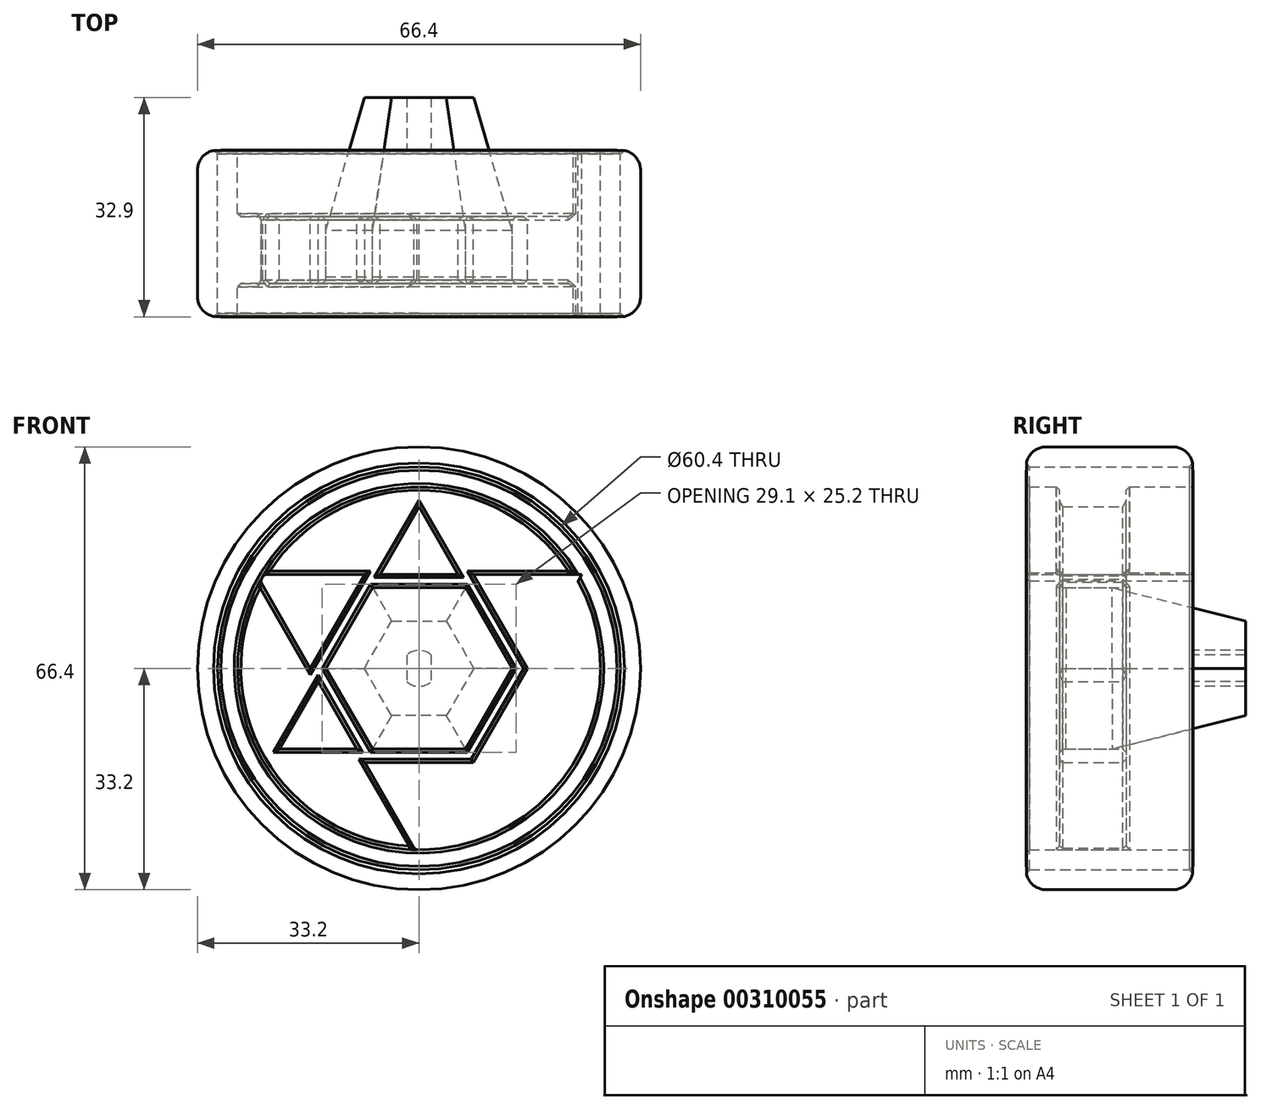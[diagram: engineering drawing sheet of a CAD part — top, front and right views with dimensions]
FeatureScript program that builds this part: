
annotation { "Feature Type Name" : "Feature", "Feature Type Description" : "" }
export const myFeature = defineFeature(function(context is Context, id is Id, definition is map)
    precondition{}
    {
        {
            var Q0;
            Q0=qCreatedBy(makeId("Front.planeOp"),FACE);
            var sketch = newSketch(context, id + "F0", { "sketchPlane" : qUnion([Q0])});
            skCircle(sketch, "E0", {"center": v(0, 0) * mm, "radius": 33.2 * mm});
            skCircle(sketch, "E1.0", {"center": v(0, 0) * mm, "radius": 30.2 * mm});
            skCircle(sketch, "E2.0", {"center": v(0, 0) * mm, "radius": 28.2 * mm});
            skCircle(sketch, "E3.0", {"center": v(0, 0) * mm, "radius": 27.2 * mm});
            skCircle(sketch, "E4.cCircle", {"center": v(0, 0) * mm, "radius": 28.2 * mm, "construction": true});
            skLineSegment(sketch, "E4.0", {"start": v(0, -28.2) * mm, "end": v(-24.42, 14.1) * mm});
            skLineSegment(sketch, "E4.1", {"start": v(-24.42, 14.1) * mm, "end": v(24.42, 14.1) * mm});
            skLineSegment(sketch, "E4.2", {"start": v(24.42, 14.1) * mm, "end": v(0, -28.2) * mm});
            skLineSegment(sketch, "E5.0", {"start": v(0, 28.2) * mm, "end": v(24.42, -14.1) * mm});
            skLineSegment(sketch, "E5.1", {"start": v(24.42, -14.1) * mm, "end": v(-24.42, -14.1) * mm});
            skLineSegment(sketch, "E5.2", {"start": v(-24.42, -14.1) * mm, "end": v(0, 28.2) * mm});
            skLineSegment(sketch, "E6.0", {"start": v(0, 24.2) * mm, "end": v(20.96, -12.1) * mm});
            skLineSegment(sketch, "E6.1", {"start": v(-20.96, -12.1) * mm, "end": v(0, 24.2) * mm});
            skLineSegment(sketch, "E6.2", {"start": v(20.96, -12.1) * mm, "end": v(-20.96, -12.1) * mm});
            skLineSegment(sketch, "E7.0", {"start": v(-20.96, 12.1) * mm, "end": v(20.96, 12.1) * mm});
            skLineSegment(sketch, "E7.1", {"start": v(0, -24.2) * mm, "end": v(-20.96, 12.1) * mm});
            skLineSegment(sketch, "E7.2", {"start": v(20.96, 12.1) * mm, "end": v(0, -24.2) * mm});
            skPoint(sketch, "E8.trimOffspring.end.orphan", {"position": v(-10.48, 6.05) * mm});
            skPoint(sketch, "E9.left.start.orphan", {"position": v(-12.04, 3.35) * mm});
            skPoint(sketch, "E10.orphan", {"position": v(-12.04, -3.35) * mm});
            skPoint(sketch, "E11.left.start.orphan", {"position": v(-10.48, -6.05) * mm});
            skPoint(sketch, "E9.bottom.end.orphan", {"position": v(12.04, 3.35) * mm});
            skPoint(sketch, "E12.trimOffspring.end.orphan", {"position": v(10.48, 6.05) * mm});
            skPoint(sketch, "E11.right.start.orphan", {"position": v(10.48, -6.05) * mm});
            skPoint(sketch, "E9.top.end.orphan", {"position": v(12.04, -3.35) * mm});
            skSolve(sketch);
        }
        {
            var Q0;
            Q0=makeQuery(id+"F0.imprint","IMPRINT",FACE,{"disambiguationData":[TD([[makeQuery(id+"F0.imprint","IMPRINT",EDGE,{"derivedFrom":sQuery(id+"F0.wireOp",EDGE,"E0")}),1.0]])]});
            extrude(context, id + "F1", {"entities" : qUnion([Q0]), "depth" : 25 * mm});
        }
        {
            var Q0;
            Q0=makeQuery(id+"F0.imprint","IMPRINT",FACE,{"disambiguationData":[TD([[makeQuery(id+"F0.imprint","IMPRINT",EDGE,{"derivedFrom":sQuery(id+"F0.wireOp",EDGE,"E1.0")}),1.0]])]});
            var Q1;
            {var subQ0=sQuery(id+"F0.wireOp",EDGE,"E4.1");var subQ5=sQuery(id+"F0.wireOp",EDGE,"E3.0");var subQ6=makeQuery(id+"F0.imprint","INTERSECT",VERTEX,{"disambiguationData":[OD(0.0)],"derivedFrom":[subQ5,subQ0]});Q1=makeQuery(id+"F0.imprint","IMPRINT",FACE,{"disambiguationData":[TD([[makeQuery(id+"F0.imprint","IMPRINT",EDGE,{"disambiguationData":[TD([[subQ6,-1.0]])],"derivedFrom":subQ5}),-1.0]])]});}
            var Q2;
            {var subQ3=sQuery(id+"F0.wireOp",EDGE,"E5.2");var subQ5=sQuery(id+"F0.wireOp",EDGE,"E3.0");var subQ6=makeQuery(id+"F0.imprint","INTERSECT",VERTEX,{"disambiguationData":[OD(0.0)],"derivedFrom":[subQ5,subQ3]});Q2=makeQuery(id+"F0.imprint","IMPRINT",FACE,{"disambiguationData":[TD([[makeQuery(id+"F0.imprint","IMPRINT",EDGE,{"disambiguationData":[TD([[subQ6,-1.0]])],"derivedFrom":subQ5}),-1.0]])]});}
            var Q3;
            {var subQ0=sQuery(id+"F0.wireOp",EDGE,"E4.0");var subQ5=sQuery(id+"F0.wireOp",EDGE,"E3.0");var subQ6=makeQuery(id+"F0.imprint","INTERSECT",VERTEX,{"disambiguationData":[OD(0.0)],"derivedFrom":[subQ5,subQ0]});Q3=makeQuery(id+"F0.imprint","IMPRINT",FACE,{"disambiguationData":[TD([[makeQuery(id+"F0.imprint","IMPRINT",EDGE,{"disambiguationData":[TD([[subQ6,-1.0]])],"derivedFrom":subQ5}),-1.0]])]});}
            var Q4;
            {var subQ3=sQuery(id+"F0.wireOp",EDGE,"E5.1");var subQ5=sQuery(id+"F0.wireOp",EDGE,"E3.0");var subQ7=makeQuery(id+"F0.imprint","INTERSECT",VERTEX,{"disambiguationData":[OD(0.0)],"derivedFrom":[subQ5,subQ3]});Q4=makeQuery(id+"F0.imprint","IMPRINT",FACE,{"disambiguationData":[TD([[makeQuery(id+"F0.imprint","IMPRINT",EDGE,{"disambiguationData":[TD([[subQ7,-1.0]])],"derivedFrom":subQ5}),-1.0]])]});}
            var Q5;
            {var subQ0=sQuery(id+"F0.wireOp",EDGE,"E4.2");var subQ5=sQuery(id+"F0.wireOp",EDGE,"E3.0");var subQ6=makeQuery(id+"F0.imprint","INTERSECT",VERTEX,{"disambiguationData":[OD(1.0)],"derivedFrom":[subQ5,subQ0]});Q5=makeQuery(id+"F0.imprint","IMPRINT",FACE,{"disambiguationData":[TD([[makeQuery(id+"F0.imprint","IMPRINT",EDGE,{"disambiguationData":[TD([[subQ6,-1.0]])],"derivedFrom":subQ5}),-1.0]])]});}
            var Q6;
            {var subQ0=sQuery(id+"F0.wireOp",EDGE,"E4.2");var subQ5=sQuery(id+"F0.wireOp",EDGE,"E3.0");var subQ6=makeQuery(id+"F0.imprint","INTERSECT",VERTEX,{"disambiguationData":[OD(0.0)],"derivedFrom":[subQ5,subQ0]});Q6=makeQuery(id+"F0.imprint","IMPRINT",FACE,{"disambiguationData":[TD([[makeQuery(id+"F0.imprint","IMPRINT",EDGE,{"disambiguationData":[TD([[subQ6,1.0]])],"derivedFrom":subQ5}),-1.0]])]});}
            var Q7;
            {var subQ0=sQuery(id+"F0.wireOp",EDGE,"E5.1");var subQ1=sQuery(id+"F0.wireOp",EDGE,"E3.0");var subQ2=makeQuery(id+"F0.imprint","INTERSECT",VERTEX,{"disambiguationData":[OD(1.0)],"derivedFrom":[subQ1,subQ0]});Q7=makeQuery(id+"F0.imprint","IMPRINT",FACE,{"disambiguationData":[TD([[makeQuery(id+"F0.imprint","IMPRINT",EDGE,{"disambiguationData":[TD([[subQ2,-1.0]])],"derivedFrom":subQ1}),-1.0]])]});}
            var Q8;
            {var subQ0=sQuery(id+"F0.wireOp",EDGE,"E4.0");var subQ1=sQuery(id+"F0.wireOp",EDGE,"E3.0");var subQ2=makeQuery(id+"F0.imprint","INTERSECT",VERTEX,{"disambiguationData":[OD(1.0)],"derivedFrom":[subQ1,subQ0]});Q8=makeQuery(id+"F0.imprint","IMPRINT",FACE,{"disambiguationData":[TD([[makeQuery(id+"F0.imprint","IMPRINT",EDGE,{"disambiguationData":[TD([[subQ2,-1.0]])],"derivedFrom":subQ1}),-1.0]])]});}
            var Q9;
            {var subQ0=sQuery(id+"F0.wireOp",EDGE,"E4.1");var subQ1=sQuery(id+"F0.wireOp",EDGE,"E3.0");var subQ2=makeQuery(id+"F0.imprint","INTERSECT",VERTEX,{"disambiguationData":[OD(0.0)],"derivedFrom":[subQ1,subQ0]});Q9=makeQuery(id+"F0.imprint","IMPRINT",FACE,{"disambiguationData":[TD([[makeQuery(id+"F0.imprint","IMPRINT",EDGE,{"disambiguationData":[TD([[subQ2,1.0]])],"derivedFrom":subQ1}),-1.0]])]});}
            var Q10;
            {var subQ0=sQuery(id+"F0.wireOp",EDGE,"E5.0");var subQ1=sQuery(id+"F0.wireOp",EDGE,"E3.0");var subQ2=makeQuery(id+"F0.imprint","INTERSECT",VERTEX,{"disambiguationData":[OD(0.0)],"derivedFrom":[subQ1,subQ0]});Q10=makeQuery(id+"F0.imprint","IMPRINT",FACE,{"disambiguationData":[TD([[makeQuery(id+"F0.imprint","IMPRINT",EDGE,{"disambiguationData":[TD([[subQ2,-1.0]])],"derivedFrom":subQ1}),-1.0]])]});}
            var Q11;
            {var subQ0=sQuery(id+"F0.wireOp",EDGE,"E4.1");var subQ1=sQuery(id+"F0.wireOp",EDGE,"E3.0");var subQ2=makeQuery(id+"F0.imprint","INTERSECT",VERTEX,{"disambiguationData":[OD(1.0)],"derivedFrom":[subQ1,subQ0]});Q11=makeQuery(id+"F0.imprint","IMPRINT",FACE,{"disambiguationData":[TD([[makeQuery(id+"F0.imprint","IMPRINT",EDGE,{"disambiguationData":[TD([[subQ2,-1.0]])],"derivedFrom":subQ1}),-1.0]])]});}
            var Q12;
            {var subQ0=sQuery(id+"F0.wireOp",EDGE,"E5.2");var subQ1=sQuery(id+"F0.wireOp",EDGE,"E3.0");var subQ2=makeQuery(id+"F0.imprint","INTERSECT",VERTEX,{"disambiguationData":[OD(1.0)],"derivedFrom":[subQ1,subQ0]});Q12=makeQuery(id+"F0.imprint","IMPRINT",FACE,{"disambiguationData":[TD([[makeQuery(id+"F0.imprint","IMPRINT",EDGE,{"disambiguationData":[TD([[subQ2,-1.0]])],"derivedFrom":subQ1}),-1.0]])]});}
            extrude(context, id + "F2", {"entities" : qUnion([Q0, Q1, Q2, Q3, Q4, Q5, Q6, Q7, Q8, Q9, Q10, Q11, Q12]), "depth" : 25 * mm});
        }
        {
            var Q0;
            {var subQ3=sQuery(id+"F0.wireOp",EDGE,"E5.0");var subQ7=sQuery(id+"F0.wireOp",EDGE,"E3.0");var subQ8=makeQuery(id+"F0.imprint","INTERSECT",VERTEX,{"disambiguationData":[OD(0.0)],"derivedFrom":[subQ7,subQ3]});Q0=makeQuery(id+"F0.imprint","IMPRINT",FACE,{"disambiguationData":[TD([[makeQuery(id+"F0.imprint","IMPRINT",EDGE,{"disambiguationData":[TD([[subQ8,-1.0]])],"derivedFrom":subQ7}),1.0]])]});}
            var Q1;
            {var subQ1=sQuery(id+"F0.wireOp",EDGE,"E4.1");var subQ6=sQuery(id+"F0.wireOp",EDGE,"E3.0");var subQ12=makeQuery(id+"F0.imprint","INTERSECT",VERTEX,{"disambiguationData":[OD(0.0)],"derivedFrom":[subQ6,subQ1]});Q1=makeQuery(id+"F0.imprint","IMPRINT",FACE,{"disambiguationData":[TD([[makeQuery(id+"F0.imprint","IMPRINT",EDGE,{"disambiguationData":[TD([[subQ12,1.0]])],"derivedFrom":subQ6}),1.0]])]});}
            var Q2;
            {var subQ0=sQuery(id+"F0.wireOp",EDGE,"E6.0");var subQ1=sQuery(id+"F0.wireOp",EDGE,"E4.1");var subQ2=makeQuery(id+"F0.imprint","INTERSECT",VERTEX,{"derivedFrom":[subQ1,subQ0]});Q2=makeQuery(id+"F0.imprint","IMPRINT",FACE,{"disambiguationData":[TD([[makeQuery(id+"F0.imprint","IMPRINT",EDGE,{"disambiguationData":[TD([[subQ2,-1.0]])],"derivedFrom":subQ1}),-1.0]])]});}
            var Q3;
            {var subQ1=sQuery(id+"F0.wireOp",EDGE,"E3.0");var subQ7=sQuery(id+"F0.wireOp",EDGE,"E5.2");var subQ11=makeQuery(id+"F0.imprint","INTERSECT",VERTEX,{"disambiguationData":[OD(1.0)],"derivedFrom":[subQ1,subQ7]});Q3=makeQuery(id+"F0.imprint","IMPRINT",FACE,{"disambiguationData":[TD([[makeQuery(id+"F0.imprint","IMPRINT",EDGE,{"disambiguationData":[TD([[subQ11,-1.0]])],"derivedFrom":subQ1}),1.0]])]});}
            var Q4;
            {var subQ0=sQuery(id+"F0.wireOp",EDGE,"E5.1");var subQ1=sQuery(id+"F0.wireOp",EDGE,"E4.0");var subQ2=makeQuery(id+"F0.imprint","INTERSECT",VERTEX,{"derivedFrom":[subQ1,subQ0]});Q4=makeQuery(id+"F0.imprint","IMPRINT",FACE,{"disambiguationData":[TD([[makeQuery(id+"F0.imprint","IMPRINT",EDGE,{"disambiguationData":[TD([[subQ2,-1.0]])],"derivedFrom":subQ1}),-1.0]])]});}
            var Q5;
            {var subQ5=sQuery(id+"F0.wireOp",EDGE,"E4.0");var subQ6=sQuery(id+"F0.wireOp",EDGE,"E3.0");var subQ7=makeQuery(id+"F0.imprint","INTERSECT",VERTEX,{"disambiguationData":[OD(1.0)],"derivedFrom":[subQ6,subQ5]});Q5=makeQuery(id+"F0.imprint","IMPRINT",FACE,{"disambiguationData":[TD([[makeQuery(id+"F0.imprint","IMPRINT",EDGE,{"disambiguationData":[TD([[subQ7,-1.0]])],"derivedFrom":subQ6}),1.0]])]});}
            var Q6;
            {var subQ0=sQuery(id+"F0.wireOp",EDGE,"E5.2");var subQ1=sQuery(id+"F0.wireOp",EDGE,"E4.1");var subQ2=makeQuery(id+"F0.imprint","INTERSECT",VERTEX,{"derivedFrom":[subQ1,subQ0]});Q6=makeQuery(id+"F0.imprint","IMPRINT",FACE,{"disambiguationData":[TD([[makeQuery(id+"F0.imprint","IMPRINT",EDGE,{"disambiguationData":[TD([[subQ2,-1.0]])],"derivedFrom":subQ1}),-1.0]])]});}
            var Q7;
            {var subQ0=sQuery(id+"F0.wireOp",EDGE,"E6.1");var subQ1=sQuery(id+"F0.wireOp",EDGE,"E4.0");var subQ2=makeQuery(id+"F0.imprint","INTERSECT",VERTEX,{"derivedFrom":[subQ1,subQ0]});Q7=makeQuery(id+"F0.imprint","IMPRINT",FACE,{"disambiguationData":[TD([[makeQuery(id+"F0.imprint","IMPRINT",EDGE,{"disambiguationData":[TD([[subQ2,-1.0]])],"derivedFrom":subQ1}),-1.0]])]});}
            var Q8;
            {var subQ0=sQuery(id+"F0.wireOp",EDGE,"E7.1");var subQ1=sQuery(id+"F0.wireOp",EDGE,"E5.2");var subQ2=makeQuery(id+"F0.imprint","INTERSECT",VERTEX,{"derivedFrom":[subQ1,subQ0]});Q8=makeQuery(id+"F0.imprint","IMPRINT",FACE,{"disambiguationData":[TD([[makeQuery(id+"F0.imprint","IMPRINT",EDGE,{"disambiguationData":[TD([[subQ2,-1.0]])],"derivedFrom":subQ1}),-1.0]])]});}
            var Q9;
            {var subQ0=sQuery(id+"F0.wireOp",EDGE,"E6.0");var subQ1=sQuery(id+"F0.wireOp",EDGE,"E4.2");var subQ2=makeQuery(id+"F0.imprint","INTERSECT",VERTEX,{"derivedFrom":[subQ1,subQ0]});Q9=makeQuery(id+"F0.imprint","IMPRINT",FACE,{"disambiguationData":[TD([[makeQuery(id+"F0.imprint","IMPRINT",EDGE,{"disambiguationData":[TD([[subQ2,-1.0]])],"derivedFrom":subQ1}),-1.0]])]});}
            var Q10;
            {var subQ0=sQuery(id+"F0.wireOp",EDGE,"E5.0");var subQ1=sQuery(id+"F0.wireOp",EDGE,"E4.2");var subQ2=makeQuery(id+"F0.imprint","INTERSECT",VERTEX,{"derivedFrom":[subQ1,subQ0]});Q10=makeQuery(id+"F0.imprint","IMPRINT",FACE,{"disambiguationData":[TD([[makeQuery(id+"F0.imprint","IMPRINT",EDGE,{"disambiguationData":[TD([[subQ2,-1.0]])],"derivedFrom":subQ1}),-1.0]])]});}
            var Q11;
            {var subQ0=sQuery(id+"F0.wireOp",EDGE,"E6.2");var subQ1=sQuery(id+"F0.wireOp",EDGE,"E4.2");var subQ2=makeQuery(id+"F0.imprint","INTERSECT",VERTEX,{"derivedFrom":[subQ1,subQ0]});Q11=makeQuery(id+"F0.imprint","IMPRINT",FACE,{"disambiguationData":[TD([[makeQuery(id+"F0.imprint","IMPRINT",EDGE,{"disambiguationData":[TD([[subQ2,-1.0]])],"derivedFrom":subQ1}),-1.0]])]});}
            var Q12;
            {var subQ0=sQuery(id+"F0.wireOp",EDGE,"E7.0");var subQ1=sQuery(id+"F0.wireOp",EDGE,"E5.0");var subQ2=makeQuery(id+"F0.imprint","INTERSECT",VERTEX,{"derivedFrom":[subQ1,subQ0]});Q12=makeQuery(id+"F0.imprint","IMPRINT",FACE,{"disambiguationData":[TD([[makeQuery(id+"F0.imprint","IMPRINT",EDGE,{"disambiguationData":[TD([[subQ2,-1.0]])],"derivedFrom":subQ1}),-1.0]])]});}
            var Q13;
            {var subQ0=sQuery(id+"F0.wireOp",EDGE,"E6.1");var subQ1=sQuery(id+"F0.wireOp",EDGE,"E4.1");var subQ2=makeQuery(id+"F0.imprint","INTERSECT",VERTEX,{"derivedFrom":[subQ1,subQ0]});Q13=makeQuery(id+"F0.imprint","IMPRINT",FACE,{"disambiguationData":[TD([[makeQuery(id+"F0.imprint","IMPRINT",EDGE,{"disambiguationData":[TD([[subQ2,-1.0]])],"derivedFrom":subQ1}),-1.0]])]});}
            var Q14;
            {var subQ1=sQuery(id+"F0.wireOp",EDGE,"E3.0");var subQ7=sQuery(id+"F0.wireOp",EDGE,"E4.1");var subQ8=makeQuery(id+"F0.imprint","INTERSECT",VERTEX,{"disambiguationData":[OD(1.0)],"derivedFrom":[subQ1,subQ7]});Q14=makeQuery(id+"F0.imprint","IMPRINT",FACE,{"disambiguationData":[TD([[makeQuery(id+"F0.imprint","IMPRINT",EDGE,{"disambiguationData":[TD([[subQ8,-1.0]])],"derivedFrom":subQ1}),1.0]])]});}
            var Q15;
            {var subQ1=sQuery(id+"F0.wireOp",EDGE,"E3.0");var subQ9=sQuery(id+"F0.wireOp",EDGE,"E5.1");var subQ11=makeQuery(id+"F0.imprint","INTERSECT",VERTEX,{"disambiguationData":[OD(1.0)],"derivedFrom":[subQ1,subQ9]});Q15=makeQuery(id+"F0.imprint","IMPRINT",FACE,{"disambiguationData":[TD([[makeQuery(id+"F0.imprint","IMPRINT",EDGE,{"disambiguationData":[TD([[subQ11,-1.0]])],"derivedFrom":subQ1}),1.0]])]});}
            var Q16;
            {var subQ0=sQuery(id+"F0.wireOp",EDGE,"E7.2");var subQ1=sQuery(id+"F0.wireOp",EDGE,"E5.1");var subQ2=makeQuery(id+"F0.imprint","INTERSECT",VERTEX,{"derivedFrom":[subQ1,subQ0]});Q16=makeQuery(id+"F0.imprint","IMPRINT",FACE,{"disambiguationData":[TD([[makeQuery(id+"F0.imprint","IMPRINT",EDGE,{"disambiguationData":[TD([[subQ2,-1.0]])],"derivedFrom":subQ1}),-1.0]])]});}
            var Q17;
            {var subQ0=sQuery(id+"F0.wireOp",EDGE,"E6.2");var subQ1=sQuery(id+"F0.wireOp",EDGE,"E4.0");var subQ2=makeQuery(id+"F0.imprint","INTERSECT",VERTEX,{"derivedFrom":[subQ1,subQ0]});Q17=makeQuery(id+"F0.imprint","IMPRINT",FACE,{"disambiguationData":[TD([[makeQuery(id+"F0.imprint","IMPRINT",EDGE,{"disambiguationData":[TD([[subQ2,-1.0]])],"derivedFrom":subQ1}),-1.0]])]});}
            extrude(context, id + "F3", {"entities" : qUnion([Q0, Q1, Q2, Q3, Q4, Q5, Q6, Q7, Q8, Q9, Q10, Q11, Q12, Q13, Q14, Q15, Q16, Q17]), "operationType" : NewBodyOperationType.ADD, "depth" : 20 * mm});
        }
        {
            var Q0;
            {var subQ0=sQuery(id+"F0.wireOp",EDGE,"E6.2");var subQ1=sQuery(id+"F0.wireOp",EDGE,"E4.0");var subQ2=makeQuery(id+"F0.imprint","INTERSECT",VERTEX,{"derivedFrom":[subQ1,subQ0]});Q0=makeQuery(id+"F0.imprint","IMPRINT",FACE,{"disambiguationData":[TD([[makeQuery(id+"F0.imprint","IMPRINT",EDGE,{"disambiguationData":[TD([[subQ2,-1.0]])],"derivedFrom":subQ1}),-1.0]])]});}
            var Q1;
            {var subQ0=sQuery(id+"F0.wireOp",EDGE,"E6.1");var subQ1=sQuery(id+"F0.wireOp",EDGE,"E4.0");var subQ2=makeQuery(id+"F0.imprint","INTERSECT",VERTEX,{"derivedFrom":[subQ1,subQ0]});Q1=makeQuery(id+"F0.imprint","IMPRINT",FACE,{"disambiguationData":[TD([[makeQuery(id+"F0.imprint","IMPRINT",EDGE,{"disambiguationData":[TD([[subQ2,-1.0]])],"derivedFrom":subQ1}),-1.0]])]});}
            var Q2;
            {var subQ1=sQuery(id+"F0.wireOp",EDGE,"E3.0");var subQ7=sQuery(id+"F0.wireOp",EDGE,"E5.2");var subQ11=makeQuery(id+"F0.imprint","INTERSECT",VERTEX,{"disambiguationData":[OD(1.0)],"derivedFrom":[subQ1,subQ7]});Q2=makeQuery(id+"F0.imprint","IMPRINT",FACE,{"disambiguationData":[TD([[makeQuery(id+"F0.imprint","IMPRINT",EDGE,{"disambiguationData":[TD([[subQ11,-1.0]])],"derivedFrom":subQ1}),1.0]])]});}
            var Q3;
            {var subQ0=sQuery(id+"F0.wireOp",EDGE,"E5.1");var subQ1=sQuery(id+"F0.wireOp",EDGE,"E4.0");var subQ2=makeQuery(id+"F0.imprint","INTERSECT",VERTEX,{"derivedFrom":[subQ1,subQ0]});Q3=makeQuery(id+"F0.imprint","IMPRINT",FACE,{"disambiguationData":[TD([[makeQuery(id+"F0.imprint","IMPRINT",EDGE,{"disambiguationData":[TD([[subQ2,-1.0]])],"derivedFrom":subQ1}),-1.0]])]});}
            var Q4;
            {var subQ5=sQuery(id+"F0.wireOp",EDGE,"E4.0");var subQ6=sQuery(id+"F0.wireOp",EDGE,"E3.0");var subQ7=makeQuery(id+"F0.imprint","INTERSECT",VERTEX,{"disambiguationData":[OD(1.0)],"derivedFrom":[subQ6,subQ5]});Q4=makeQuery(id+"F0.imprint","IMPRINT",FACE,{"disambiguationData":[TD([[makeQuery(id+"F0.imprint","IMPRINT",EDGE,{"disambiguationData":[TD([[subQ7,-1.0]])],"derivedFrom":subQ6}),1.0]])]});}
            var Q5;
            {var subQ0=sQuery(id+"F0.wireOp",EDGE,"E7.2");var subQ1=sQuery(id+"F0.wireOp",EDGE,"E5.1");var subQ2=makeQuery(id+"F0.imprint","INTERSECT",VERTEX,{"derivedFrom":[subQ1,subQ0]});Q5=makeQuery(id+"F0.imprint","IMPRINT",FACE,{"disambiguationData":[TD([[makeQuery(id+"F0.imprint","IMPRINT",EDGE,{"disambiguationData":[TD([[subQ2,-1.0]])],"derivedFrom":subQ1}),-1.0]])]});}
            var Q6;
            {var subQ0=sQuery(id+"F0.wireOp",EDGE,"E6.2");var subQ1=sQuery(id+"F0.wireOp",EDGE,"E4.2");var subQ2=makeQuery(id+"F0.imprint","INTERSECT",VERTEX,{"derivedFrom":[subQ1,subQ0]});Q6=makeQuery(id+"F0.imprint","IMPRINT",FACE,{"disambiguationData":[TD([[makeQuery(id+"F0.imprint","IMPRINT",EDGE,{"disambiguationData":[TD([[subQ2,-1.0]])],"derivedFrom":subQ1}),-1.0]])]});}
            var Q7;
            {var subQ1=sQuery(id+"F0.wireOp",EDGE,"E3.0");var subQ9=sQuery(id+"F0.wireOp",EDGE,"E5.1");var subQ11=makeQuery(id+"F0.imprint","INTERSECT",VERTEX,{"disambiguationData":[OD(1.0)],"derivedFrom":[subQ1,subQ9]});Q7=makeQuery(id+"F0.imprint","IMPRINT",FACE,{"disambiguationData":[TD([[makeQuery(id+"F0.imprint","IMPRINT",EDGE,{"disambiguationData":[TD([[subQ11,-1.0]])],"derivedFrom":subQ1}),1.0]])]});}
            var Q8;
            {var subQ0=sQuery(id+"F0.wireOp",EDGE,"E6.0");var subQ1=sQuery(id+"F0.wireOp",EDGE,"E4.2");var subQ2=makeQuery(id+"F0.imprint","INTERSECT",VERTEX,{"derivedFrom":[subQ1,subQ0]});Q8=makeQuery(id+"F0.imprint","IMPRINT",FACE,{"disambiguationData":[TD([[makeQuery(id+"F0.imprint","IMPRINT",EDGE,{"disambiguationData":[TD([[subQ2,-1.0]])],"derivedFrom":subQ1}),-1.0]])]});}
            var Q9;
            {var subQ0=sQuery(id+"F0.wireOp",EDGE,"E5.0");var subQ1=sQuery(id+"F0.wireOp",EDGE,"E4.2");var subQ2=makeQuery(id+"F0.imprint","INTERSECT",VERTEX,{"derivedFrom":[subQ1,subQ0]});Q9=makeQuery(id+"F0.imprint","IMPRINT",FACE,{"disambiguationData":[TD([[makeQuery(id+"F0.imprint","IMPRINT",EDGE,{"disambiguationData":[TD([[subQ2,-1.0]])],"derivedFrom":subQ1}),-1.0]])]});}
            var Q10;
            {var subQ0=sQuery(id+"F0.wireOp",EDGE,"E7.1");var subQ1=sQuery(id+"F0.wireOp",EDGE,"E5.2");var subQ2=makeQuery(id+"F0.imprint","INTERSECT",VERTEX,{"derivedFrom":[subQ1,subQ0]});Q10=makeQuery(id+"F0.imprint","IMPRINT",FACE,{"disambiguationData":[TD([[makeQuery(id+"F0.imprint","IMPRINT",EDGE,{"disambiguationData":[TD([[subQ2,-1.0]])],"derivedFrom":subQ1}),-1.0]])]});}
            var Q11;
            {var subQ1=sQuery(id+"F0.wireOp",EDGE,"E3.0");var subQ7=sQuery(id+"F0.wireOp",EDGE,"E4.1");var subQ8=makeQuery(id+"F0.imprint","INTERSECT",VERTEX,{"disambiguationData":[OD(1.0)],"derivedFrom":[subQ1,subQ7]});Q11=makeQuery(id+"F0.imprint","IMPRINT",FACE,{"disambiguationData":[TD([[makeQuery(id+"F0.imprint","IMPRINT",EDGE,{"disambiguationData":[TD([[subQ8,-1.0]])],"derivedFrom":subQ1}),1.0]])]});}
            var Q12;
            {var subQ0=sQuery(id+"F0.wireOp",EDGE,"E5.2");var subQ1=sQuery(id+"F0.wireOp",EDGE,"E4.1");var subQ2=makeQuery(id+"F0.imprint","INTERSECT",VERTEX,{"derivedFrom":[subQ1,subQ0]});Q12=makeQuery(id+"F0.imprint","IMPRINT",FACE,{"disambiguationData":[TD([[makeQuery(id+"F0.imprint","IMPRINT",EDGE,{"disambiguationData":[TD([[subQ2,-1.0]])],"derivedFrom":subQ1}),-1.0]])]});}
            var Q13;
            {var subQ0=sQuery(id+"F0.wireOp",EDGE,"E6.1");var subQ1=sQuery(id+"F0.wireOp",EDGE,"E4.1");var subQ2=makeQuery(id+"F0.imprint","INTERSECT",VERTEX,{"derivedFrom":[subQ1,subQ0]});Q13=makeQuery(id+"F0.imprint","IMPRINT",FACE,{"disambiguationData":[TD([[makeQuery(id+"F0.imprint","IMPRINT",EDGE,{"disambiguationData":[TD([[subQ2,-1.0]])],"derivedFrom":subQ1}),-1.0]])]});}
            var Q14;
            {var subQ3=sQuery(id+"F0.wireOp",EDGE,"E5.0");var subQ7=sQuery(id+"F0.wireOp",EDGE,"E3.0");var subQ8=makeQuery(id+"F0.imprint","INTERSECT",VERTEX,{"disambiguationData":[OD(0.0)],"derivedFrom":[subQ7,subQ3]});Q14=makeQuery(id+"F0.imprint","IMPRINT",FACE,{"disambiguationData":[TD([[makeQuery(id+"F0.imprint","IMPRINT",EDGE,{"disambiguationData":[TD([[subQ8,-1.0]])],"derivedFrom":subQ7}),1.0]])]});}
            var Q15;
            {var subQ0=sQuery(id+"F0.wireOp",EDGE,"E6.0");var subQ1=sQuery(id+"F0.wireOp",EDGE,"E4.1");var subQ2=makeQuery(id+"F0.imprint","INTERSECT",VERTEX,{"derivedFrom":[subQ1,subQ0]});Q15=makeQuery(id+"F0.imprint","IMPRINT",FACE,{"disambiguationData":[TD([[makeQuery(id+"F0.imprint","IMPRINT",EDGE,{"disambiguationData":[TD([[subQ2,-1.0]])],"derivedFrom":subQ1}),-1.0]])]});}
            var Q16;
            {var subQ0=sQuery(id+"F0.wireOp",EDGE,"E7.0");var subQ1=sQuery(id+"F0.wireOp",EDGE,"E5.0");var subQ2=makeQuery(id+"F0.imprint","INTERSECT",VERTEX,{"derivedFrom":[subQ1,subQ0]});Q16=makeQuery(id+"F0.imprint","IMPRINT",FACE,{"disambiguationData":[TD([[makeQuery(id+"F0.imprint","IMPRINT",EDGE,{"disambiguationData":[TD([[subQ2,-1.0]])],"derivedFrom":subQ1}),-1.0]])]});}
            var Q17;
            {var subQ1=sQuery(id+"F0.wireOp",EDGE,"E4.1");var subQ6=sQuery(id+"F0.wireOp",EDGE,"E3.0");var subQ12=makeQuery(id+"F0.imprint","INTERSECT",VERTEX,{"disambiguationData":[OD(0.0)],"derivedFrom":[subQ6,subQ1]});Q17=makeQuery(id+"F0.imprint","IMPRINT",FACE,{"disambiguationData":[TD([[makeQuery(id+"F0.imprint","IMPRINT",EDGE,{"disambiguationData":[TD([[subQ12,1.0]])],"derivedFrom":subQ6}),1.0]])]});}
            extrude(context, id + "F4", {"entities" : qUnion([Q0, Q1, Q2, Q3, Q4, Q5, Q6, Q7, Q8, Q9, Q10, Q11, Q12, Q13, Q14, Q15, Q16, Q17]), "operationType" : NewBodyOperationType.REMOVE, "depth" : 10 * mm});
        }
        {
            var Q0;
            Q0=makeQuery(id+"F1.opExtrude","SWEPT_FACE",FACE,{"disambiguationData":[OSD([sQuery(id+"F0.wireOp",EDGE,"E0")])]});
            fillet(context, id + "F5", {"entities" : qUnion([Q0]), "radius" : 3 * mm, "tangentPropagation" : true, "allowEdgeOverflow" : false});
        }
        {
            var Q0;
            Q0=makeQuery(id+"F2.opExtrude","CAP_EDGE",EDGE,{"disambiguationData":[OSD([sQuery(id+"F0.wireOp",EDGE,"E1.0")])],"isStart":false});
            var Q1;
            Q1=makeQuery(id+"F2.opExtrude","CAP_EDGE",EDGE,{"disambiguationData":[OSD([sQuery(id+"F0.wireOp",EDGE,"E1.0")])],"isStart":true});
            chamfer(context, id + "F6", {"entities" : qUnion([Q0, Q1]), "width" : .5 * mm, "tangentPropagation" : true});
        }
        {
            var Q0;
            Q0=makeQuery(id+"F5.opFillet","BLEND_EDGE",EDGE,{"blendedFrom":[makeQuery(id+"F1.opExtrude","CAP_EDGE",EDGE,{"disambiguationData":[OSD([sQuery(id+"F0.wireOp",EDGE,"E0")])],"isStart":false}),makeQuery(id+"F1.opExtrude","SWEPT_FACE",FACE,{"disambiguationData":[OSD([sQuery(id+"F0.wireOp",EDGE,"E1.0")])]})],"blendedInto":[makeQuery(id+"F1.opExtrude","SWEPT_FACE",FACE,{"disambiguationData":[OSD([sQuery(id+"F0.wireOp",EDGE,"E1.0")])]})]});
            var Q1;
            Q1=makeQuery(id+"F5.opFillet","BLEND_EDGE",EDGE,{"blendedFrom":[makeQuery(id+"F1.opExtrude","CAP_EDGE",EDGE,{"disambiguationData":[OSD([sQuery(id+"F0.wireOp",EDGE,"E0")])],"isStart":true}),makeQuery(id+"F1.opExtrude","SWEPT_FACE",FACE,{"disambiguationData":[OSD([sQuery(id+"F0.wireOp",EDGE,"E1.0")])]})],"blendedInto":[makeQuery(id+"F1.opExtrude","SWEPT_FACE",FACE,{"disambiguationData":[OSD([sQuery(id+"F0.wireOp",EDGE,"E1.0")])]})]});
            chamfer(context, id + "F7", {"entities" : qUnion([Q0, Q1]), "width" : .5 * mm, "tangentPropagation" : true});
        }
        {
            var Q0;
            Q0=makeQuery(id+"F2.opExtrude","CAP_EDGE",EDGE,{"disambiguationData":[OSD([sQuery(id+"F0.wireOp",EDGE,"E3.0")])],"isStart":false});
            var Q1;
            Q1=makeQuery(id+"F3.opExtrude","CAP_FACE",FACE,{"disambiguationData":[OSD([sQuery(id+"F0.wireOp",EDGE,"E3.0"),sQuery(id+"F0.wireOp",EDGE,"E4.0"),sQuery(id+"F0.wireOp",EDGE,"E4.1"),sQuery(id+"F0.wireOp",EDGE,"E4.2"),sQuery(id+"F0.wireOp",EDGE,"E5.0"),sQuery(id+"F0.wireOp",EDGE,"E5.1"),sQuery(id+"F0.wireOp",EDGE,"E5.2"),sQuery(id+"F0.wireOp",EDGE,"E6.0"),sQuery(id+"F0.wireOp",EDGE,"E6.1"),sQuery(id+"F0.wireOp",EDGE,"E6.2"),sQuery(id+"F0.wireOp",EDGE,"E7.0"),sQuery(id+"F0.wireOp",EDGE,"E7.1"),sQuery(id+"F0.wireOp",EDGE,"E7.2")])],"isStart":false});
            var Q2;
            Q2=makeQuery(id+"F4.boolean.opBoolean","COPY",FACE,{"derivedFrom":makeQuery(id+"F4.opExtrude","CAP_FACE",FACE,{"disambiguationData":[OSD([sQuery(id+"F0.wireOp",EDGE,"E3.0"),sQuery(id+"F0.wireOp",EDGE,"E4.0"),sQuery(id+"F0.wireOp",EDGE,"E4.1"),sQuery(id+"F0.wireOp",EDGE,"E4.2"),sQuery(id+"F0.wireOp",EDGE,"E5.0"),sQuery(id+"F0.wireOp",EDGE,"E5.1"),sQuery(id+"F0.wireOp",EDGE,"E5.2"),sQuery(id+"F0.wireOp",EDGE,"E6.0"),sQuery(id+"F0.wireOp",EDGE,"E6.1"),sQuery(id+"F0.wireOp",EDGE,"E6.2"),sQuery(id+"F0.wireOp",EDGE,"E7.0"),sQuery(id+"F0.wireOp",EDGE,"E7.1"),sQuery(id+"F0.wireOp",EDGE,"E7.2")])],"isStart":false})});
            var Q3;
            {var subQ0=sQuery(id+"F0.wireOp",EDGE,"E5.1");var subQ1=sQuery(id+"F0.wireOp",EDGE,"E3.0");var subQ2=makeQuery(id+"F0.imprint","INTERSECT",VERTEX,{"disambiguationData":[OD(1.0)],"derivedFrom":[subQ1,subQ0]});var subQ3=sQuery(id+"F0.wireOp",EDGE,"E5.0");var subQ5=sQuery(id+"F0.wireOp",EDGE,"E4.0");var subQ6=makeQuery(id+"F0.imprint","INTERSECT",VERTEX,{"disambiguationData":[OD(1.0)],"derivedFrom":[subQ1,subQ5]});var subQ7=sQuery(id+"F0.wireOp",EDGE,"E4.2");var subQ8=makeQuery(id+"F0.imprint","INTERSECT",VERTEX,{"disambiguationData":[OD(1.0)],"derivedFrom":[subQ1,subQ7]});var subQ9=sQuery(id+"F0.wireOp",EDGE,"E5.2");var subQ10=makeQuery(id+"F0.imprint","INTERSECT",VERTEX,{"disambiguationData":[OD(1.0)],"derivedFrom":[subQ1,subQ9]});var subQ12=sQuery(id+"F0.wireOp",EDGE,"E4.1");var subQ13=makeQuery(id+"F0.imprint","INTERSECT",VERTEX,{"disambiguationData":[OD(1.0)],"derivedFrom":[subQ1,subQ12]});var subQ14=makeQuery(id+"F0.imprint","INTERSECT",VERTEX,{"disambiguationData":[OD(0.0)],"derivedFrom":[subQ1,subQ5]});var subQ15=makeQuery(id+"F0.imprint","INTERSECT",VERTEX,{"disambiguationData":[OD(0.0)],"derivedFrom":[subQ1,subQ3]});var subQ17=makeQuery(id+"F0.imprint","INTERSECT",VERTEX,{"disambiguationData":[OD(0.0)],"derivedFrom":[subQ1,subQ12]});var subQ18=makeQuery(id+"F0.imprint","INTERSECT",VERTEX,{"disambiguationData":[OD(0.0)],"derivedFrom":[subQ1,subQ7]});var subQ23=makeQuery(id+"F2.opExtrude","CAP_EDGE",EDGE,{"disambiguationData":[OSD([subQ1])],"isStart":true});Q3=makeQuery(id+"F4.boolean.opBoolean","MERGE",EDGE,{"derivedFrom":[makeQuery(id+"F3.boolean.opBoolean","SPLIT",EDGE,{"disambiguationData":[TD([makeQuery(id+"F3.opExtrude","SWEPT_FACE",FACE,{"disambiguationData":[OSD([subQ12]),TDD([makeQuery(id+"F0.imprint","IMPRINT",EDGE,{"disambiguationData":[TD([[subQ17,1.0]])],"derivedFrom":subQ12})])]})])],"derivedFrom":subQ23}),makeQuery(id+"F3.boolean.opBoolean","SPLIT",EDGE,{"disambiguationData":[TD([makeQuery(id+"F3.opExtrude","SWEPT_FACE",FACE,{"disambiguationData":[OSD([subQ7]),TDD([makeQuery(id+"F0.imprint","IMPRINT",EDGE,{"disambiguationData":[TD([[subQ18,-1.0]])],"derivedFrom":subQ7})])]})])],"derivedFrom":subQ23}),makeQuery(id+"F3.boolean.opBoolean","SPLIT",EDGE,{"disambiguationData":[TD([makeQuery(id+"F3.opExtrude","SWEPT_FACE",FACE,{"disambiguationData":[OSD([subQ12]),TDD([makeQuery(id+"F0.imprint","IMPRINT",EDGE,{"disambiguationData":[TD([[subQ13,-1.0]])],"derivedFrom":subQ12})])]})])],"derivedFrom":subQ23}),makeQuery(id+"F3.boolean.opBoolean","SPLIT",EDGE,{"disambiguationData":[TD([makeQuery(id+"F3.opExtrude","SWEPT_FACE",FACE,{"disambiguationData":[OSD([subQ5]),TDD([makeQuery(id+"F0.imprint","IMPRINT",EDGE,{"disambiguationData":[TD([[subQ14,1.0]])],"derivedFrom":subQ5})])]})])],"derivedFrom":subQ23}),makeQuery(id+"F3.boolean.opBoolean","SPLIT",EDGE,{"disambiguationData":[TD([makeQuery(id+"F3.opExtrude","SWEPT_FACE",FACE,{"disambiguationData":[OSD([subQ5]),TDD([makeQuery(id+"F0.imprint","IMPRINT",EDGE,{"disambiguationData":[TD([[subQ6,-1.0]])],"derivedFrom":subQ5})])]})])],"derivedFrom":subQ23}),makeQuery(id+"F3.boolean.opBoolean","SPLIT",EDGE,{"disambiguationData":[TD([makeQuery(id+"F3.opExtrude","SWEPT_FACE",FACE,{"disambiguationData":[OSD([subQ7]),TDD([makeQuery(id+"F0.imprint","IMPRINT",EDGE,{"disambiguationData":[TD([[subQ8,1.0]])],"derivedFrom":subQ7})])]})])],"derivedFrom":subQ23}),makeQuery(id+"F4.opExtrude","CAP_EDGE",EDGE,{"disambiguationData":[OSD([subQ1]),TDD([makeQuery(id+"F0.imprint","IMPRINT",EDGE,{"disambiguationData":[TD([[subQ17,1.0]])],"derivedFrom":subQ1})])],"isStart":true}),makeQuery(id+"F4.opExtrude","CAP_EDGE",EDGE,{"disambiguationData":[OSD([subQ1]),TDD([makeQuery(id+"F0.imprint","IMPRINT",EDGE,{"disambiguationData":[TD([[subQ15,-1.0]])],"derivedFrom":subQ1})])],"isStart":true}),makeQuery(id+"F4.opExtrude","CAP_EDGE",EDGE,{"disambiguationData":[OSD([subQ1]),TDD([makeQuery(id+"F0.imprint","IMPRINT",EDGE,{"disambiguationData":[TD([[subQ13,-1.0]])],"derivedFrom":subQ1})])],"isStart":true}),makeQuery(id+"F4.opExtrude","CAP_EDGE",EDGE,{"disambiguationData":[OSD([subQ1]),TDD([makeQuery(id+"F0.imprint","IMPRINT",EDGE,{"disambiguationData":[TD([[subQ10,-1.0]])],"derivedFrom":subQ1})])],"isStart":true}),makeQuery(id+"F4.opExtrude","CAP_EDGE",EDGE,{"disambiguationData":[OSD([subQ1]),TDD([makeQuery(id+"F0.imprint","IMPRINT",EDGE,{"disambiguationData":[TD([[subQ6,-1.0]])],"derivedFrom":subQ1})])],"isStart":true}),makeQuery(id+"F4.opExtrude","CAP_EDGE",EDGE,{"disambiguationData":[OSD([subQ1]),TDD([makeQuery(id+"F0.imprint","IMPRINT",EDGE,{"disambiguationData":[TD([[subQ2,-1.0]])],"derivedFrom":subQ1})])],"isStart":true})]});}
            chamfer(context, id + "F8", {"entities" : qUnion([Q0, Q1, Q2, Q3]), "width" : .5 * mm, "tangentPropagation" : true});
        }
        {
            var Q0;
            {var subQ0=sQuery(id+"F0.wireOp",EDGE,"E7.0");var subQ1=sQuery(id+"F0.wireOp",EDGE,"E6.0");var subQ2=makeQuery(id+"F0.imprint","INTERSECT",VERTEX,{"derivedFrom":[subQ1,subQ0]});Q0=makeQuery(id+"F0.imprint","IMPRINT",FACE,{"disambiguationData":[TD([[makeQuery(id+"F0.imprint","IMPRINT",EDGE,{"disambiguationData":[TD([[subQ2,-1.0]])],"derivedFrom":subQ1}),-1.0]])]});}
            extrude(context, id + "F9", {"entities" : qUnion([Q0]), "depth" : 19 * mm});
        }
        {
            var Q0;
            Q0=makeQuery(id+"F9.opExtrude","CAP_FACE",FACE,{"disambiguationData":[OSD([sQuery(id+"F0.wireOp",EDGE,"E6.0"),sQuery(id+"F0.wireOp",EDGE,"E6.1"),sQuery(id+"F0.wireOp",EDGE,"E6.2"),sQuery(id+"F0.wireOp",EDGE,"E7.0"),sQuery(id+"F0.wireOp",EDGE,"E7.1"),sQuery(id+"F0.wireOp",EDGE,"E7.2")])],"isStart":true});
            var sketch = newSketch(context, id + "F10", { "sketchPlane" : qUnion([Q0])});
            skCircle(sketch, "E13", {"center": v(0, 0) * mm, "radius": 2.7 * mm});
            skLineSegment(sketch, "E14", {"start": v(-1.8, 2.01) * mm, "end": v(-1.8, -2.01) * mm});
            skLineSegment(sketch, "E15", {"start": v(1.8, 2.01) * mm, "end": v(1.8, -2.01) * mm});
            skSolve(sketch);
        }
        {
            var Q0;
            Q0=makeQuery(id+"F10.imprint","IMPRINT",FACE,{"disambiguationData":[TD([[makeQuery(id+"F10.imprint","IMPRINT",EDGE,{"derivedFrom":makeQuery(id+"F9.opExtrude","CAP_EDGE",EDGE,{"disambiguationData":[OSD([sQuery(id+"F0.wireOp",EDGE,"E6.0")])],"isStart":true})}),1.0]])]});
            var Q1;
            {var subQ0=sQuery(id+"F10.wireOp",EDGE,"E14");Q1=makeQuery(id+"F10.imprint","IMPRINT",FACE,{"disambiguationData":[TD([[makeQuery(id+"F10.imprint","IMPRINT",EDGE,{"derivedFrom":subQ0}),-1.0]])]});}
            var Q2;
            {var subQ0=sQuery(id+"F10.wireOp",EDGE,"E15");Q2=makeQuery(id+"F10.imprint","IMPRINT",FACE,{"disambiguationData":[TD([[makeQuery(id+"F10.imprint","IMPRINT",EDGE,{"derivedFrom":subQ0}),1.0]])]});}
            extrude(context, id + "F11", {"entities" : qUnion([Q0, Q1, Q2]), "operationType" : NewBodyOperationType.ADD, "depth" : 7.9 * mm});
        }
        {
            var Q0;
            Q0=makeQuery(id+"F11.opExtrude","CAP_EDGE",EDGE,{"disambiguationData":[OSD([sQuery(id+"F0.wireOp",EDGE,"E7.1")])],"isStart":false});
            var Q1;
            Q1=makeQuery(id+"F11.opExtrude","CAP_EDGE",EDGE,{"disambiguationData":[OSD([sQuery(id+"F0.wireOp",EDGE,"E6.1")])],"isStart":false});
            var Q2;
            Q2=makeQuery(id+"F11.opExtrude","CAP_EDGE",EDGE,{"disambiguationData":[OSD([sQuery(id+"F0.wireOp",EDGE,"E7.0")])],"isStart":false});
            var Q3;
            Q3=makeQuery(id+"F11.opExtrude","CAP_EDGE",EDGE,{"disambiguationData":[OSD([sQuery(id+"F0.wireOp",EDGE,"E6.0")])],"isStart":false});
            var Q4;
            Q4=makeQuery(id+"F11.opExtrude","CAP_EDGE",EDGE,{"disambiguationData":[OSD([sQuery(id+"F0.wireOp",EDGE,"E7.2")])],"isStart":false});
            var Q5;
            Q5=makeQuery(id+"F11.opExtrude","CAP_EDGE",EDGE,{"disambiguationData":[OSD([sQuery(id+"F0.wireOp",EDGE,"E6.2")])],"isStart":false});
            chamfer(context, id + "F12", {"entities" : qUnion([Q0, Q1, Q2, Q3, Q4, Q5]), "chamferType" : ChamferType.TWO_OFFSETS, "width1" : 5 * mm, "oppositeDirection" : false, "width2" : 20 * mm, "tangentPropagation" : true});
        }
    });
